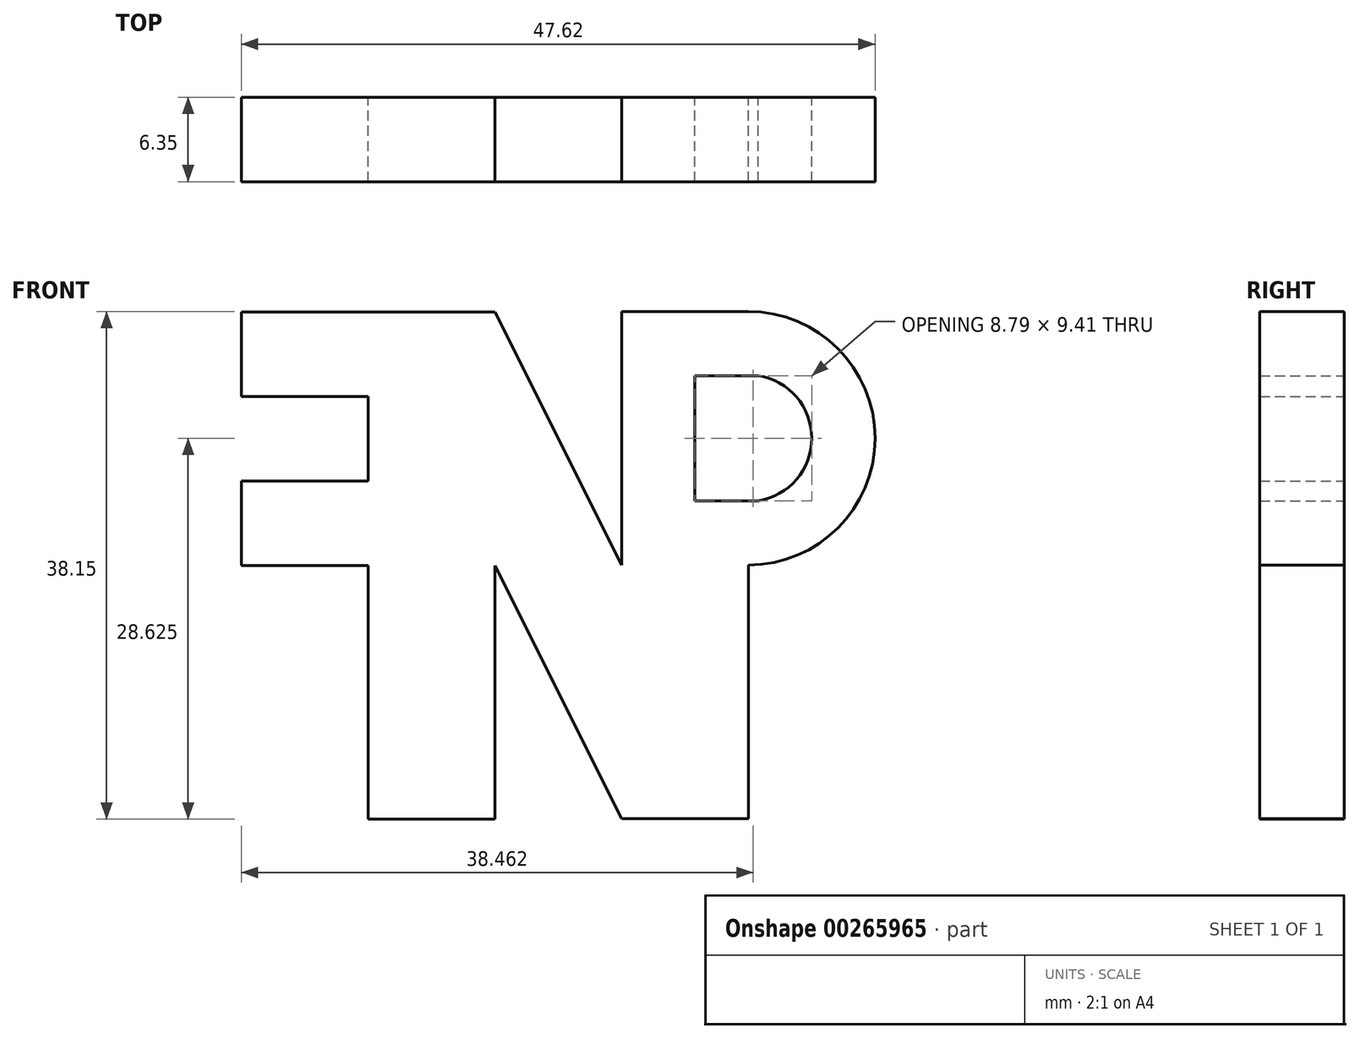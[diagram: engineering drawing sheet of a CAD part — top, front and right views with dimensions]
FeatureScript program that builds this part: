
annotation { "Feature Type Name" : "Feature", "Feature Type Description" : "" }
export const myFeature = defineFeature(function(context is Context, id is Id, definition is map)
    precondition{}
    {
        {
            var Q0;
            Q0=qCreatedBy(makeId("Front.planeOp"),FACE);
            var sketch = newSketch(context, id + "F0", { "sketchPlane" : qUnion([Q0])});
            skLineSegment(sketch, "E0", {"start": v(-28.58, 29.5) * mm, "end": v(-19.05, 29.5) * mm});
            skLineSegment(sketch, "E1", {"start": v(-28.57, 29.5) * mm, "end": v(-28.57, 23.15) * mm});
            skLineSegment(sketch, "E2", {"start": v(-28.57, 23.15) * mm, "end": v(-19.05, 23.15) * mm});
            skLineSegment(sketch, "E3", {"start": v(-19.05, 23.15) * mm, "end": v(-19.05, 16.8) * mm});
            skLineSegment(sketch, "E4", {"start": v(-19.05, 16.8) * mm, "end": v(-28.57, 16.8) * mm});
            skLineSegment(sketch, "E5", {"start": v(-28.57, 16.8) * mm, "end": v(-28.57, 10.45) * mm});
            skLineSegment(sketch, "E6", {"start": v(-28.57, 10.45) * mm, "end": v(-19.05, 10.45) * mm});
            skLineSegment(sketch, "E7", {"start": v(-19.05, 10.45) * mm, "end": v(-19.05, -8.6) * mm});
            skLineSegment(sketch, "E8", {"start": v(-19.05, -8.6) * mm, "end": v(-9.52, -8.6) * mm});
            skLineSegment(sketch, "E9", {"start": v(9.53, 10.5) * mm, "end": v(9.53, -8.55) * mm});
            skLineSegment(sketch, "E10", {"start": v(9.53, 29.55) * mm, "end": v(0, 29.55) * mm});
            skLineSegment(sketch, "E11", {"start": v(9.53, 29.55) * mm, "end": v(9.53, 29.55) * mm});
            skLineSegment(sketch, "E12", {"start": v(19.05, 20.03) * mm, "end": v(19.05, 20.03) * mm});
            skLineSegment(sketch, "E13", {"start": v(9.53, 10.5) * mm, "end": v(9.53, 10.5) * mm});
            skPoint(sketch, "E14.visualSharp", {"position": v(19.05, 29.55) * mm});
            skArc(sketch, "E14.filletArc", {"start": v(19.05, 20.03) * mm, "mid": v(16.26, 26.76) * mm, "end": v(9.53, 29.55) * mm});
            skPoint(sketch, "E15.visualSharp", {"position": v(19.05, 10.5) * mm});
            skArc(sketch, "E15.filletArc", {"start": v(9.53, 10.5) * mm, "mid": v(16.26, 13.3) * mm, "end": v(19.05, 20.03) * mm});
            skLineSegment(sketch, "E16", {"start": v(-19.05, 29.5) * mm, "end": v(-9.53, 29.5) * mm});
            skLineSegment(sketch, "E17", {"start": v(-9.52, -8.6) * mm, "end": v(-9.52, 10.45) * mm});
            skLineSegment(sketch, "E18", {"start": v(-9.53, 10.45) * mm, "end": v(0, -8.55) * mm});
            skLineSegment(sketch, "E19", {"start": v(0, -8.55) * mm, "end": v(9.53, -8.55) * mm});
            skLineSegment(sketch, "E20", {"start": v(-9.53, 29.5) * mm, "end": v(0, 10.5) * mm});
            skLineSegment(sketch, "E21", {"start": v(0, 29.55) * mm, "end": v(0, 10.5) * mm});
            skArc(sketch, "E22.0", {"start": v(14.29, 20.03) * mm, "mid": v(13.14, 23.12) * mm, "end": v(10.26, 24.73) * mm});
            skArc(sketch, "E23.0", {"start": v(10.26, 15.32) * mm, "mid": v(13.14, 16.93) * mm, "end": v(14.29, 20.03) * mm});
            skPoint(sketch, "E24.endSnap0", {"position": v(13.14, 23.12) * mm});
            skLineSegment(sketch, "E25", {"start": v(10.26, 24.73) * mm, "end": v(5.5, 24.73) * mm});
            skLineSegment(sketch, "E26", {"start": v(5.5, 24.73) * mm, "end": v(5.5, 15.32) * mm});
            skLineSegment(sketch, "E27", {"start": v(5.5, 15.32) * mm, "end": v(10.26, 15.32) * mm});
            skLineSegment(sketch, "E28", {"start": v(0, 29.55) * mm, "end": v(0, 28.8) * mm});
            skLineSegment(sketch, "E29", {"start": v(2.38, 31.18) * mm, "end": v(2.38, 29.55) * mm});
            skPoint(sketch, "E30.visualSharp", {"position": v(-11.9, 34.36) * mm});
            skPoint(sketch, "E31.visualSharp", {"position": v(-9.53, 31.98) * mm});
            skSolve(sketch);
        }
        {
            var Q0;
            {var subQ2=sQuery(id+"F0.wireOp",EDGE,"E0");Q0=makeQuery(id+"F0.imprint","IMPRINT",FACE,{"disambiguationData":[TD([[makeQuery(id+"F0.imprint","IMPRINT",EDGE,{"derivedFrom":subQ2}),-1.0]])]});}
            extrude(context, id + "F1", {"entities" : qUnion([Q0]), "depth" : 6.35 * mm});
        }
    });
